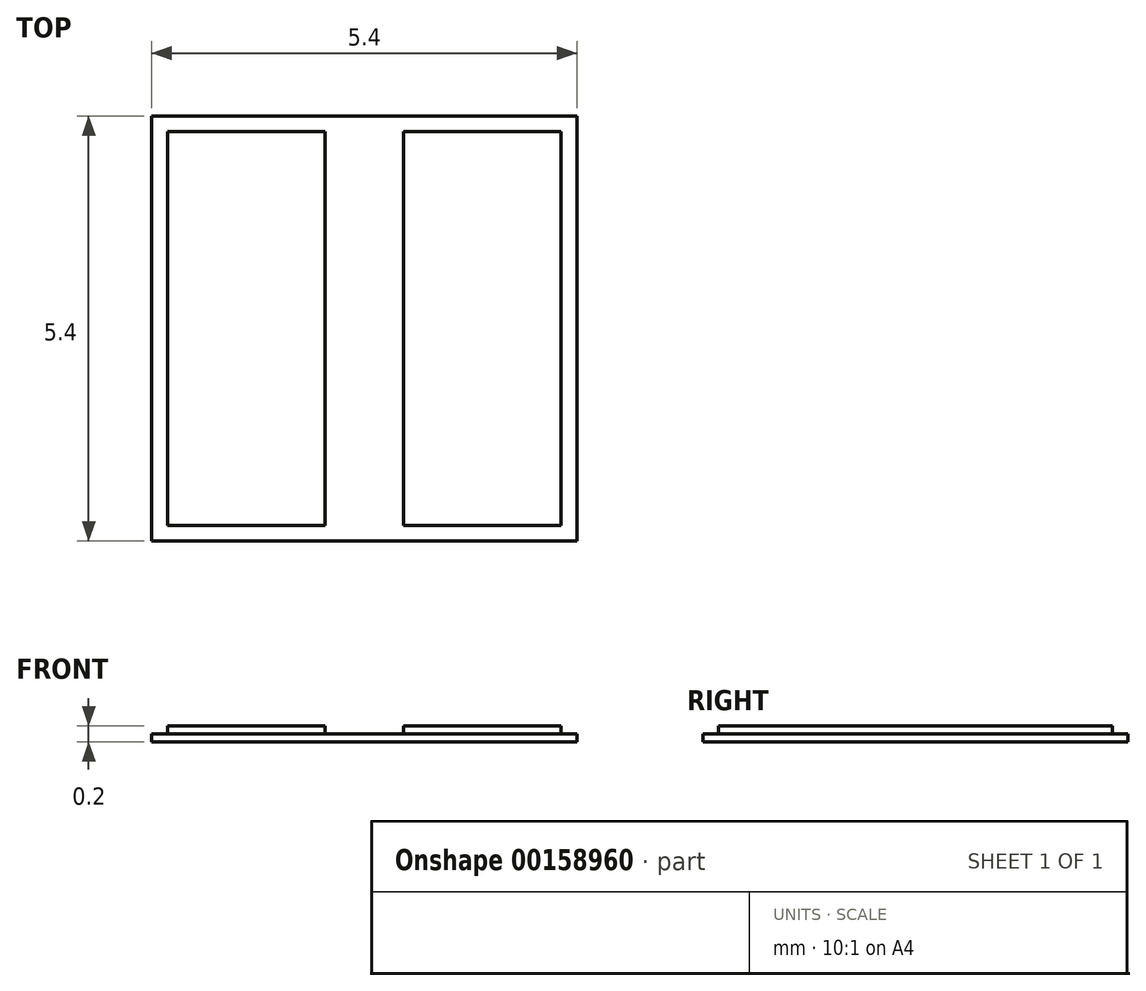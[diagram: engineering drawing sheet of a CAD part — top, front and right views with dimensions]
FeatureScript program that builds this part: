
annotation { "Feature Type Name" : "Feature", "Feature Type Description" : "" }
export const myFeature = defineFeature(function(context is Context, id is Id, definition is map)
    precondition{}
    {
        {
            var Q0;
            Q0=qCreatedBy(makeId("Top.planeOp"),FACE);
            var sketch = newSketch(context, id + "F0", { "sketchPlane" : qUnion([Q0])});
            skLineSegment(sketch, "E0.bottom", {"start": v(-0.5, -2.5) * mm, "end": v(-2.5, -2.5) * mm});
            skLineSegment(sketch, "E0.top", {"start": v(-0.5, 2.5) * mm, "end": v(-2.5, 2.5) * mm});
            skLineSegment(sketch, "E0.left", {"start": v(-0.5, -2.5) * mm, "end": v(-0.5, 2.5) * mm});
            skLineSegment(sketch, "E0.right", {"start": v(-2.5, -2.5) * mm, "end": v(-2.5, 2.5) * mm});
            skPoint(sketch, "E0.middle", {"position": v(0, 0) * mm});
            skLineSegment(sketch, "E1.MirrorCS", {"start": v(0.5, -2.5) * mm, "end": v(2.5, -2.5) * mm});
            skLineSegment(sketch, "E2.MirrorCS", {"start": v(0.5, 2.5) * mm, "end": v(2.5, 2.5) * mm});
            skLineSegment(sketch, "E3.MirrorCS", {"start": v(2.5, -2.5) * mm, "end": v(2.5, 2.5) * mm});
            skLineSegment(sketch, "E4.MirrorCS", {"start": v(0.5, -2.5) * mm, "end": v(0.5, 2.5) * mm});
            skLineSegment(sketch, "E5.bottom", {"start": v(-2.7, 2.7) * mm, "end": v(2.7, 2.7) * mm});
            skLineSegment(sketch, "E5.top", {"start": v(-2.7, -2.7) * mm, "end": v(2.7, -2.7) * mm});
            skLineSegment(sketch, "E5.left", {"start": v(-2.7, 2.7) * mm, "end": v(-2.7, -2.7) * mm});
            skLineSegment(sketch, "E5.right", {"start": v(2.7, 2.7) * mm, "end": v(2.7, -2.7) * mm});
            skLineSegment(sketch, "E6", {"start": v(-2.7, -2.7) * mm, "end": v(2.7, 2.7) * mm, "construction": true});
            skLineSegment(sketch, "E7", {"start": v(2.7, -2.7) * mm, "end": v(-2.7, 2.7) * mm, "construction": true});
            skLineSegment(sketch, "E8", {"start": v(-4.88, 0) * mm, "end": v(6.05, 0) * mm, "construction": true});
            skPoint(sketch, "E8.endSnap0", {"position": v(2.7, 0) * mm});
            skSolve(sketch);
        }
        {
            var Q0;
            Q0=makeQuery(id+"F0.imprint","IMPRINT",FACE,{"disambiguationData":[TD([[makeQuery(id+"F0.imprint","IMPRINT",EDGE,{"derivedFrom":sQuery(id+"F0.wireOp",EDGE,"E0.bottom")}),-1.0]])]});
            var Q1;
            Q1=makeQuery(id+"F0.imprint","IMPRINT",FACE,{"disambiguationData":[TD([[makeQuery(id+"F0.imprint","IMPRINT",EDGE,{"derivedFrom":sQuery(id+"F0.wireOp",EDGE,"E0.bottom")}),1.0]])]});
            var Q2;
            Q2=makeQuery(id+"F0.imprint","IMPRINT",FACE,{"disambiguationData":[TD([[makeQuery(id+"F0.imprint","IMPRINT",EDGE,{"derivedFrom":sQuery(id+"F0.wireOp",EDGE,"E1.MirrorCS")}),1.0]])]});
            extrude(context, id + "F1", {"entities" : qUnion([Q0, Q1, Q2]), "oppositeDirection" : true, "depth" : 0.1 * mm});
        }
        {
            var Q0;
            Q0=makeQuery(id+"F0.imprint","IMPRINT",FACE,{"disambiguationData":[TD([[makeQuery(id+"F0.imprint","IMPRINT",EDGE,{"derivedFrom":sQuery(id+"F0.wireOp",EDGE,"E0.bottom")}),-1.0]])]});
            var Q1;
            Q1=makeQuery(id+"F0.imprint","IMPRINT",FACE,{"disambiguationData":[TD([[makeQuery(id+"F0.imprint","IMPRINT",EDGE,{"derivedFrom":sQuery(id+"F0.wireOp",EDGE,"E1.MirrorCS")}),1.0]])]});
            extrude(context, id + "F2", {"entities" : qUnion([Q0, Q1]), "depth" : 0.1 * mm});
        }
    });
